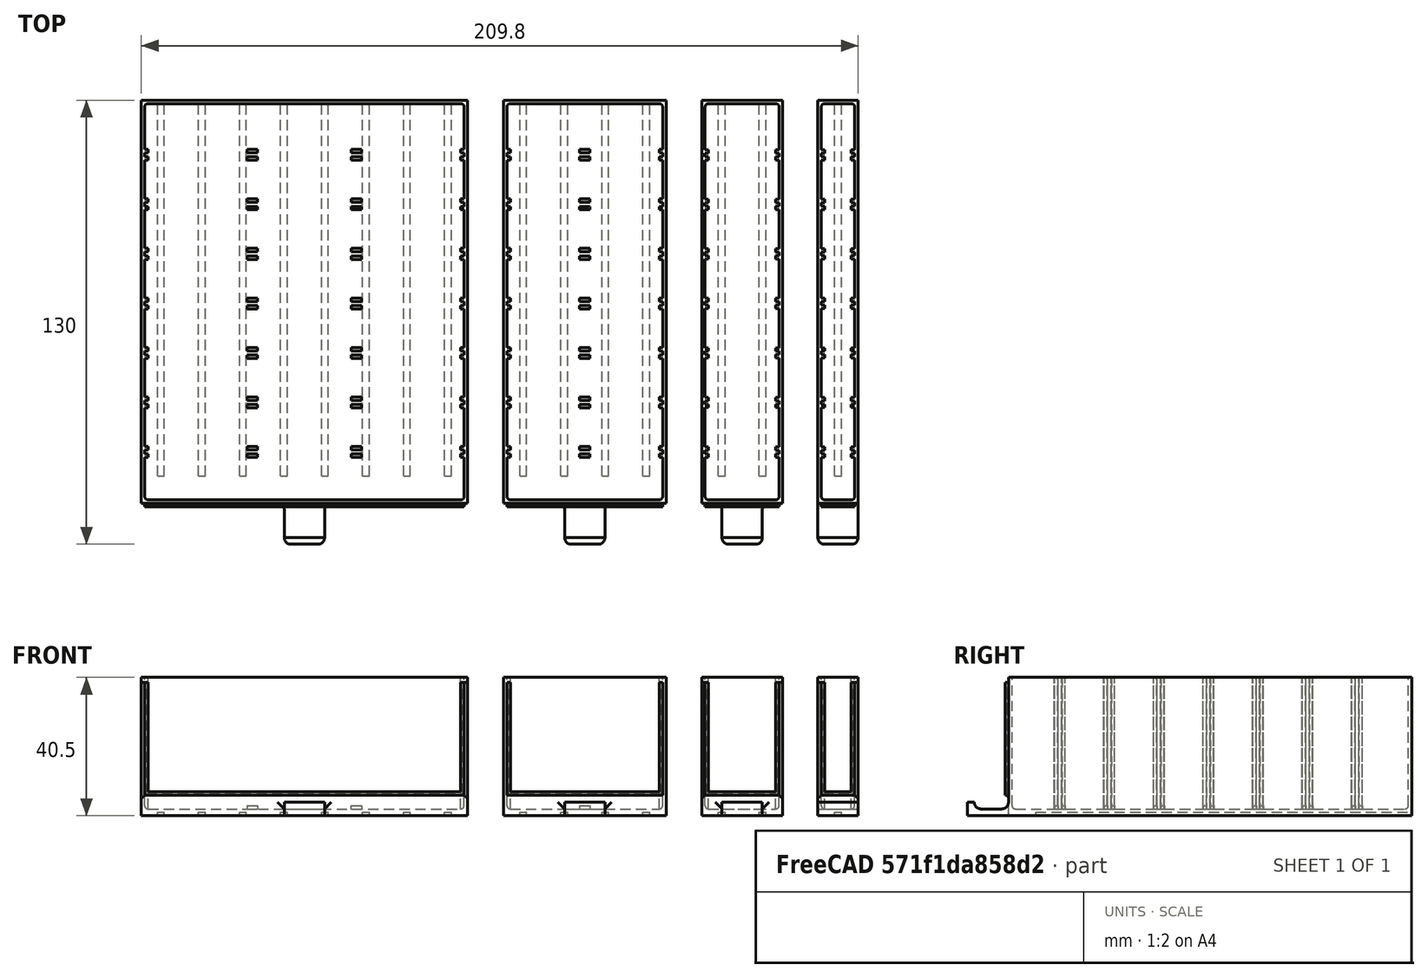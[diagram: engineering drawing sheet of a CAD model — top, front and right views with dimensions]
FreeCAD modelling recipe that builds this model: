
FCSTD DOCUMENT  (FreeCAD 0.16R)
Label: 1story_drawers
License: All rights reserved
LicenseURL: http://en.wikipedia.org/wiki/All_rights_reserved
objects: Part::Box×46, Part::Cut×23, Part::Fillet×19, Part::MultiFuse×19, Part::FeaturePython×8
note: 115 computed .brp shape members not serialized (recipe doc carries the construction recipe); baked Part::Feature solids carry a one-line shape summary decoded from their .brp

FEATURE [Part::Box] Box  label="outer_box"
  Height = 40.5
  Length = 95.5
  Width = 118
FEATURE [Part::Box] Box001  label="inner_box"
  Height = 39.5
  Length = 93.5
  Placement = pos=(1,1,2) rot=(0,0,1;0rad)
  Width = 116
FEATURE [Part::Fillet] Fillet
  Base = -> Box001
  Edges = 8 edges r=1: [Edge1,Edge3,Edge4,Edge5,Edge7,Edge8,Edge9,Edge11]
FEATURE [Part::Cut] Cut  label="Guideless Drawer"
  Base = -> Box
  Tool = -> Fillet
FEATURE [Part::Box] Box004  label="Guide"
  Height = 1
  Length = 2
  Placement = pos=(0,8,0) rot=(0,0,1;0rad)
  Width = 110
FEATURE [Part::FeaturePython] Array  label="Guide array"  # Draft array (typed FeaturePython)
  Angle = 360
  ArrayType = 0
  Axis = (0,0,1)
  Base = -> Box004
  Center = (0,0,0)
  Fuse = false
  IntervalAxis = (0,0,0)
  IntervalX = (12,0,0)
  IntervalY = (0,1,0)
  IntervalZ = (0,0,0)
  NumberPolar = 1
  NumberX = 8
  NumberY = 1
  NumberZ = 1
  Placement = pos=(4.75,0,0) rot=(0,0,1;0rad)
FEATURE [Part::Box] Box006  label="Separator Holder Block"
  Height = 38.5
  Length = 93.5
  Placement = pos=(1,13.4,2) rot=(0,0,1;0rad)
  Width = 3.2
FEATURE [Part::Box] Box007  label="Separator Gap"
  Height = 38.5
  Length = 93.5
  Placement = pos=(1,14.4,2) rot=(0,0,1;0rad)
  Width = 1.2
FEATURE [Part::Box] Box008  label="Separator Holder Gap Block"
  Height = 38.5
  Length = 91.5
  Placement = pos=(2,13.4,2) rot=(0,0,1;0rad)
  Width = 3.2
FEATURE [Part::Fillet] Fillet005
  Base = -> Box006
  Edges = 2 edges r=1: [Edge4,Edge8]
FEATURE [Part::Cut] Cut002  label="Separator Holder Guides"
  Base = -> Fillet005
  Tool = -> Box007
FEATURE [Part::Cut] Cut004  label="Handlerless Guided Drawer"
  Base = -> Cut
  Tool = -> Array
FEATURE [Part::Box] Box009  label="Bottom Separator Holder Gap Block"
  Height = 1
  Length = 3
  Placement = pos=(31,13.4,2) rot=(0,0,1;0rad)
  Width = 3.2
FEATURE [Part::FeaturePython] Array001  label="Bottom Separator Gap Array"  # Draft array (typed FeaturePython)
  Angle = 360
  ArrayType = 0
  Axis = (0,0,1)
  Base = -> Box009
  Center = (0,0,0)
  Fuse = false
  IntervalAxis = (0,0,0)
  IntervalX = (30.5,0,0)
  IntervalY = (0,1,0)
  IntervalZ = (0,0,0)
  NumberPolar = 1
  NumberX = 2
  NumberY = 1
  NumberZ = 1
FEATURE [Part::Cut] Cut005  label="Separator Holder Gap"
  Base = -> Box008
  Tool = -> Array001
FEATURE [Part::Cut] Cut006  label="Separator Holder"
  Base = -> Cut002
  Tool = -> Cut005
FEATURE [Part::FeaturePython] Array002  label="Separator Holder Array"  # Draft array (typed FeaturePython)
  Angle = 360
  ArrayType = 0
  Axis = (0,0,1)
  Base = -> Cut006
  Center = (0,0,0)
  Fuse = false
  IntervalAxis = (0,0,0)
  IntervalX = (1,0,0)
  IntervalY = (0,14.5,0)
  IntervalZ = (0,0,0)
  NumberPolar = 1
  NumberX = 1
  NumberY = 7
  NumberZ = 1
FEATURE [Part::Box] Box010  label="LabelHolder_Main_Block"
  Height = 33
  Length = 93.5
  Placement = pos=(1,-1,6) rot=(0,0,1;0rad)
  Width = 1
  expr: Placement.Base.y = outer_box.Placement.Base.y - LabelHolder_Main_Block.Width
  expr: Placement.Base.x = inner_box.Placement.Base.x
  expr: Length = inner_box.Length
FEATURE [Part::Box] Box011  label="LabelHolder_Inner_Gap"
  Height = 32.5
  Length = 92.5
  Placement = pos=(1.5,-0.5,6.5) rot=(0,0,1;0rad)
  Width = 0.5
  expr: Height = LabelHolder_Main_Block.Height - 0.5mm
  expr: Placement.Base.z = LabelHolder_Main_Block.Placement.Base.z + 0.5mm
  expr: Placement.Base.y = LabelHolder_Main_Block.Placement.Base.y + 0.5mm
  expr: Placement.Base.x = LabelHolder_Main_Block.Placement.Base.x + 0.5mm
  expr: Length = LabelHolder_Main_Block.Length - 1mm
FEATURE [Part::Box] Box012  label="LabelHolder_Outer_Gap"
  Height = 32
  Length = 91.5
  Placement = pos=(2,-1,7) rot=(0,0,1;0rad)
  Width = 0.5
  expr: Height = LabelHolder_Main_Block.Height - 1mm
  expr: Placement.Base.z = LabelHolder_Main_Block.Placement.Base.z + 1mm
  expr: Placement.Base.y = LabelHolder_Main_Block.Placement.Base.y
  expr: Placement.Base.x = LabelHolder_Main_Block.Placement.Base.x + 1mm
  expr: Length = LabelHolder_Main_Block.Length - 2mm
FEATURE [Part::MultiFuse] Fusion003  label="LabelHolder Gap"
  Shapes = -> [Box011,Box012]
FEATURE [Part::Cut] Cut007  label="LabelHolder"
  Base = -> Box010
  Tool = -> Fusion003
FEATURE [Part::MultiFuse] Fusion  label="Handlerless Drawer"
  Shapes = -> [Cut004,Array002]
FEATURE [Part::Box] Box013  label="Handler_block"
  Height = 2
  Length = 11.8
  Placement = pos=(41.85,-12,0) rot=(0,0,1;0rad)
  Width = 12
  expr: Placement.Base.y = outer_box.Placement.Base.y - Handler_block.Width
  expr: Placement.Base.x = outer_box.Placement.Base.x + (outer_box.Length - Handler_block.Length) / 2
FEATURE [Part::Box] Box015  label="Handler_pick"
  Height = 2
  Length = 11.8
  Placement = pos=(41.85,-12,2) rot=(0,0,1;0rad)
  Width = 2
  expr: Placement.Base.z = Handler_block.Placement.Base.z + 2mm
  expr: Placement.Base.y = Handler_block.Placement.Base.y
  expr: Placement.Base.x = Handler_block.Placement.Base.x
FEATURE [Part::MultiFuse] Fusion004
  Shapes = -> [Box015,Box013]
FEATURE [Part::Fillet] Fillet006
  Base = -> Fusion004
  Edges = 5 edges r=1.9: [Edge5,Edge8,Edge10,Edge13,Edge19]
FEATURE [Part::MultiFuse] Fusion005
  Shapes = -> [Fillet006,Fusion]
FEATURE [Part::Fillet] Fillet007  label="LabelHolderlessCabinet"
  Base = -> Fusion005
  Edges = 3 edges r=2: [Edge25,Edge34,Edge39]
FEATURE [Part::MultiFuse] Fusion006
  Shapes = -> [Cut007,Fillet007]
FEATURE [Part::Fillet] Fillet008  label="BigDrawer"
  Base = -> Fusion006
  Edges = 3 edges r=0.9: [Edge11,Edge27,Edge28]
FEATURE [Part::Box] Box016  label="outer_box001"
  Height = 40.5
  Length = 47.6
  Width = 118
FEATURE [Part::Box] Box017  label="inner_box001"
  Height = 39.5
  Length = 45.6
  Placement = pos=(1,1,2) rot=(0,0,1;0rad)
  Width = 116
FEATURE [Part::Fillet] Fillet009
  Base = -> Box017
  Edges = 8 edges r=1: [Edge1,Edge3,Edge4,Edge5,Edge7,Edge8,Edge9,Edge11]
FEATURE [Part::Cut] Cut008  label="Guideless drawer"
  Base = -> Box016
  Tool = -> Fillet009
FEATURE [Part::Box] Box018  label="Guide001"
  Height = 1
  Length = 2
  Placement = pos=(4.8,8,0) rot=(0,0,1;0rad)
  Width = 110
FEATURE [Part::FeaturePython] Array003  label="Guide Array"  # Draft array (typed FeaturePython)
  Angle = 360
  ArrayType = 0
  Axis = (0,0,1)
  Base = -> Box018
  Center = (0,0,0)
  Fuse = false
  IntervalAxis = (0,0,0)
  IntervalX = (12,0,0)
  IntervalY = (0,1,0)
  IntervalZ = (0,0,0)
  NumberPolar = 1
  NumberX = 4
  NumberY = 1
  NumberZ = 1
FEATURE [Part::Box] Box019  label="Separator Block"
  Height = 38.5
  Length = 45.6
  Placement = pos=(1,13.4,2) rot=(0,0,1;0rad)
  Width = 3.2
FEATURE [Part::Box] Box020  label="Separator Gap001"
  Height = 38.5
  Length = 45.6
  Placement = pos=(1,14.4,2) rot=(0,0,1;0rad)
  Width = 1.2
FEATURE [Part::Box] Box021  label="Separator Holder Gap Block001"
  Height = 38.5
  Length = 43.6
  Placement = pos=(2,13.4,2) rot=(0,0,1;0rad)
  Width = 3.2
FEATURE [Part::Fillet] Fillet010
  Base = -> Box019
  Edges = 2 edges r=1: [Edge4,Edge8]
FEATURE [Part::Cut] Cut009  label="Separator Holder Guides001"
  Base = -> Fillet010
  Tool = -> Box020
FEATURE [Part::Cut] Cut010  label="Separatorless Guided Drawer"
  Base = -> Cut008
  Tool = -> Array003
FEATURE [Part::Box] Box022  label="Bottom Separator Holder Gap Block001"
  Height = 1
  Length = 3
  Placement = pos=(22.3,13.4,2) rot=(0,0,1;0rad)
  Width = 3.2
FEATURE [Part::Cut] Cut011  label="Separator Holder Gap001"
  Base = -> Box021
  Tool = -> Box022
FEATURE [Part::Cut] Cut012  label="Separator Holder001"
  Base = -> Cut009
  Tool = -> Cut011
FEATURE [Part::FeaturePython] Array004  label="Separator Holder Array001"  # Draft array (typed FeaturePython)
  Angle = 360
  ArrayType = 0
  Axis = (0,0,1)
  Base = -> Cut012
  Center = (0,0,0)
  Fuse = false
  IntervalAxis = (0,0,0)
  IntervalX = (1,0,0)
  IntervalY = (0,14.5,0)
  IntervalZ = (0,0,0)
  NumberPolar = 1
  NumberX = 1
  NumberY = 7
  NumberZ = 1
FEATURE [Part::Box] Box023  label="LabelHolder_Main_Block001"
  Height = 33
  Length = 45.6
  Placement = pos=(1,-1,6) rot=(0,0,1;0rad)
  Width = 1
  expr: Placement.Base.y = outer_box.Placement.Base.y - LabelHolder_Main_Block.Width
  expr: Placement.Base.x = inner_box.Placement.Base.x
  expr: Length = inner_box.Length
FEATURE [Part::Box] Box024  label="LabelHolder_Inner_Gap001"
  Height = 32.5
  Length = 44.6
  Placement = pos=(1.5,-0.5,6.5) rot=(0,0,1;0rad)
  Width = 0.5
  expr: Placement.Base.y = LabelHolder_Main_Block.Placement.Base.y + 0.5mm
  expr: Height = LabelHolder_Main_Block.Height - 0.5mm
  expr: Placement.Base.z = LabelHolder_Main_Block.Placement.Base.z + 0.5mm
  expr: Length = inner_box.Length - 1mm
FEATURE [Part::Box] Box025  label="LabelHolder_Outer_Gap001"
  Height = 32
  Length = 43.6
  Placement = pos=(2,-1,7) rot=(0,0,1;0rad)
  Width = 0.5
  expr: Placement.Base.y = LabelHolder_Main_Block.Placement.Base.y
  expr: Placement.Base.x = LabelHolder_Main_Block.Placement.Base.x + 1mm
  expr: Length = LabelHolder_Main_Block.Length - 2mm
  expr: Height = LabelHolder_Main_Block.Height - 1mm
  expr: Placement.Base.z = LabelHolder_Main_Block.Placement.Base.z + 1mm
FEATURE [Part::MultiFuse] Fusion007  label="LabelHolder_Gap"
  Shapes = -> [Box024,Box025]
FEATURE [Part::Cut] Cut013  label="LabelHolder001"
  Base = -> Box023
  Tool = -> Fusion007
FEATURE [Part::MultiFuse] Fusion008  label="Handlerless Drawer001"
  Shapes = -> [Array004,Cut010]
FEATURE [Part::Box] Box026  label="Handler_block001"
  Height = 2
  Length = 11.8
  Placement = pos=(17.9,-12,0) rot=(0,0,1;0rad)
  Width = 12
  expr: Placement.Base.y = outer_box.Placement.Base.y - Handler_block.Width
  expr: Placement.Base.x = outer_box.Placement.Base.x + (outer_box.Length - Handler_block.Length) / 2
FEATURE [Part::Box] Box027  label="Handler_pick001"
  Height = 2
  Length = 11.8
  Placement = pos=(17.9,-12,2) rot=(0,0,1;0rad)
  Width = 2
  expr: Placement.Base.z = Handler_block.Placement.Base.z + 2mm
  expr: Placement.Base.y = Handler_block.Placement.Base.y
  expr: Placement.Base.x = Handler_block.Placement.Base.x
FEATURE [Part::MultiFuse] Fusion009
  Shapes = -> [Box026,Box027]
FEATURE [Part::Fillet] Fillet011
  Base = -> Fusion009
  Edges = 5 edges r=1.9: [Edge5,Edge11,Edge15,Edge18,Edge19]
FEATURE [Part::MultiFuse] Fusion010
  Shapes = -> [Fusion008,Fillet011]
FEATURE [Part::Fillet] Fillet012
  Base = -> Fusion010
  Edges = 3 edges r=2: [Edge627,Edge628,Edge629]
FEATURE [Part::MultiFuse] Fusion011  label="StandardDrawer"
  Placement = pos=(106,0,0) rot=(0,0,1;0rad)
  Shapes = -> [Cut013,Fillet012]
FEATURE [Part::Box] Box028  label="outer_box002"
  Height = 40.5
  Length = 23.7
  Width = 118
FEATURE [Part::Box] Box029  label="inner_box002"
  Height = 39.5
  Length = 21.7
  Placement = pos=(1,1,2) rot=(0,0,1;0rad)
  Width = 116
FEATURE [Part::Fillet] Fillet014  label="Filleted Inner Box"
  Base = -> Box029
  Edges = 8 edges r=1: [Edge1,Edge3,Edge4,Edge5,Edge7,Edge8,Edge9,Edge11]
FEATURE [Part::Cut] Cut014  label="Guideless Drawer001"
  Base = -> Box028
  Tool = -> Fillet014
FEATURE [Part::Box] Box030  label="Guide002"
  Height = 1
  Length = 2
  Placement = pos=(0,8,0) rot=(0,0,1;0rad)
  Width = 110
FEATURE [Part::FeaturePython] Array005  label="Guide array001"  # Draft array (typed FeaturePython)
  Angle = 360
  ArrayType = 0
  Axis = (0,0,1)
  Base = -> Box030
  Center = (0,0,0)
  Fuse = false
  IntervalAxis = (0,0,0)
  IntervalX = (12,0,0)
  IntervalY = (0,1,0)
  IntervalZ = (0,0,0)
  NumberPolar = 1
  NumberX = 2
  NumberY = 1
  NumberZ = 1
  Placement = pos=(4.85,0,0) rot=(0,0,1;0rad)
FEATURE [Part::Box] Box031  label="Separator Holder Gap002"
  Height = 38.5
  Length = 21.7
  Placement = pos=(1,14.5,2) rot=(0,0,1;0rad)
  Width = 1
FEATURE [Part::Box] Box032  label="Separator Block001"
  Height = 38.5
  Length = 21.7
  Placement = pos=(1,13.5,2) rot=(0,0,1;0rad)
  Width = 3
FEATURE [Part::Fillet] Fillet015  label="Filletted Separator Block"
  Base = -> Box032
  Edges = 2 edges r=1: [Edge4,Edge8]
FEATURE [Part::Box] Box033  label="Separator Gap002"
  Height = 38.5
  Length = 19.7
  Placement = pos=(2,13.5,2) rot=(0,0,1;0rad)
  Width = 3
FEATURE [Part::Cut] Cut015
  Base = -> Fillet015
  Tool = -> Box033
FEATURE [Part::Cut] Cut003  label="Separator Holder002"
  Base = -> Cut015
  Tool = -> Box031
FEATURE [Part::FeaturePython] Array006  label="Separator Holders Array"  # Draft array (typed FeaturePython)
  Angle = 360
  ArrayType = 0
  Axis = (0,0,1)
  Base = -> Cut003
  Center = (0,0,0)
  Fuse = false
  IntervalAxis = (0,0,0)
  IntervalX = (1,0,0)
  IntervalY = (0,14.5,0)
  IntervalZ = (0,0,0)
  NumberPolar = 1
  NumberX = 1
  NumberY = 7
  NumberZ = 1
FEATURE [Part::Cut] Cut016  label="Guided Drawer"
  Base = -> Cut014
  Tool = -> Array005
FEATURE [Part::Box] Box034  label="LabelHolder_Main_Block002"
  Height = 33
  Length = 21.7
  Placement = pos=(1,-1,6) rot=(0,0,1;0rad)
  Width = 1
  expr: Length = inner_box.Length
  expr: Placement.Base.x = inner_box.Placement.Base.x
  expr: Placement.Base.y = outer_box.Placement.Base.y - LabelHolder_Main_Block.Width
FEATURE [Part::Box] Box035  label="LabelHolder_Inner_Gap002"
  Height = 32.5
  Length = 20.7
  Placement = pos=(1.5,-0.5,6.5) rot=(0,0,1;0rad)
  Width = 0.5
  expr: Length = LabelHolder_Main_Block.Length - 1mm
  expr: Placement.Base.x = LabelHolder_Main_Block.Placement.Base.x + (LabelHolder_Main_Block.Length - LabelHolder_Inner_Gap.Length) / 2
  expr: Placement.Base.y = LabelHolder_Main_Block.Placement.Base.y + LabelHolder_Inner_Gap.Width
  expr: Width = LabelHolder_Main_Block.Width / 2
  expr: Height = LabelHolder_Main_Block.Height - 0.5mm
  expr: Placement.Base.z = LabelHolder_Main_Block.Placement.Base.z + 0.5mm
FEATURE [Part::Box] Box036  label="LabelHolder_Outer_Gap002"
  Height = 32
  Length = 19.7
  Placement = pos=(2,-1,7) rot=(0,0,1;0rad)
  Width = 0.5
  expr: Placement.Base.y = LabelHolder_Inner_Gap.Placement.Base.y - LabelHolder_Outer_Gap.Width
  expr: Placement.Base.x = LabelHolder_Main_Block.Placement.Base.x + (LabelHolder_Main_Block.Length - LabelHolder_Outer_Gap.Length) / 2
  expr: Placement.Base.z = LabelHolder_Main_Block.Placement.Base.z + 1mm
  expr: Height = LabelHolder_Main_Block.Height - 1mm
  expr: Width = LabelHolder_Main_Block.Width / 2
  expr: Length = LabelHolder_Main_Block.Length - 2mm
FEATURE [Part::MultiFuse] Fusion012  label="LabelHolder_Gap001"
  Shapes = -> [Box035,Box036]
FEATURE [Part::Cut] Cut017  label="LabelHolder002"
  Base = -> Box034
  Tool = -> Fusion012
FEATURE [Part::MultiFuse] Fusion013  label="Handlerless Drawer002"
  Shapes = -> [Cut016,Array006]
FEATURE [Part::Box] Box037  label="Handler_block002"
  Height = 2
  Length = 11.8
  Placement = pos=(5.95,-12,0) rot=(0,0,1;0rad)
  Width = 12
  expr: Placement.Base.x = (outer_box.Length - Handler_block.Length) / 2
FEATURE [Part::Box] Box014  label="Handler_pick002"
  Height = 2
  Length = 11.8
  Placement = pos=(5.95,-12,2) rot=(0,0,1;0rad)
  Width = 2
  expr: Placement.Base.z = Handler_block.Placement.Base.z + 2mm
  expr: Placement.Base.y = Handler_block.Placement.Base.y
  expr: Placement.Base.x = Handler_block.Placement.Base.x
FEATURE [Part::MultiFuse] Fusion014
  Shapes = -> [Box014,Box037]
FEATURE [Part::Fillet] Fillet016  label="Handler"
  Base = -> Fusion014
  Edges = 5 edges r=1.9: [Edge5,Edge8,Edge10,Edge13,Edge19]
FEATURE [Part::MultiFuse] Fusion015
  Shapes = -> [Fusion013,Fillet016]
FEATURE [Part::Fillet] Fillet017  label="LabelHolderlessDrawer"
  Base = -> Fusion015
  Edges = 3 edges r=2: [Edge6,Edge7,Edge8]
FEATURE [Part::MultiFuse] Fusion016
  Shapes = -> [Cut017,Fillet017]
FEATURE [Part::Fillet] Fillet018  label="SmallDrawer"
  Base = -> Fusion016
  Edges = 3 edges r=0.9: [Edge11,Edge27,Edge28]
  Placement = pos=(164,0,0) rot=(0,0,1;0rad)
FEATURE [Part::Box] Box038  label="outer_box003"
  Height = 40.5
  Length = 11.8
  Width = 118
FEATURE [Part::Box] Box039  label="inner_box003"
  Height = 38.5
  Length = 9.8
  Placement = pos=(1,1,2) rot=(0,0,1;0rad)
  Width = 116
FEATURE [Part::Fillet] Fillet019
  Base = -> Box039
  Edges = 8 edges r=1: [Edge1,Edge3,Edge4,Edge5,Edge7,Edge8,Edge9,Edge11]
FEATURE [Part::Cut] Cut018  label="Guideless Drawer002"
  Base = -> Box038
  Tool = -> Fillet019
FEATURE [Part::Box] Box040  label="Guide003"
  Height = 1
  Length = 2
  Placement = pos=(4.9,8,0) rot=(0,0,1;0rad)
  Width = 110
FEATURE [Part::Box] Box041  label="Separator Holder Block Draft"
  Height = 38.5
  Length = 9.8
  Width = 3
FEATURE [Part::Box] Box042  label="Separator Gap003"
  Height = 38.5
  Length = 9.8
  Placement = pos=(0,1,0) rot=(0,0,1;0rad)
  Width = 1
FEATURE [Part::Box] Box043  label="Separator Holder Gap003"
  Height = 38.5
  Length = 7.8
  Placement = pos=(1,0,0) rot=(0,0,1;0rad)
  Width = 3
FEATURE [Part::Fillet] Fillet020
  Base = -> Box041
  Edges = 2 edges r=1: [Edge4,Edge8]
FEATURE [Part::Cut] Cut019
  Base = -> Fillet020
  Tool = -> Box042
FEATURE [Part::Cut] Cut020  label="Separator Holder Draft"
  Base = -> Cut019
  Tool = -> Box043
FEATURE [Part::FeaturePython] Array007  label="Separator Holder Array002"  # Draft array (typed FeaturePython)
  Angle = 360
  ArrayType = 0
  Axis = (0,0,1)
  Base = -> Cut020
  Center = (0,0,0)
  Fuse = false
  IntervalAxis = (0,0,0)
  IntervalX = (1,0,0)
  IntervalY = (0,14.5,0)
  IntervalZ = (0,0,0)
  NumberPolar = 1
  NumberX = 1
  NumberY = 7
  NumberZ = 1
  Placement = pos=(1,13.5,2) rot=(0,0,1;0rad)
FEATURE [Part::Cut] Cut021  label="Guided Separatorless Drawer"
  Base = -> Cut018
  Tool = -> Box040
FEATURE [Part::Box] Box044  label="labelholder_main_block"
  Height = 33
  Length = 9.8
  Placement = pos=(1,-1,6) rot=(0,0,1;0rad)
  Width = 1
FEATURE [Part::Box] Box045  label="labelholder_inner_gap"
  Height = 32.5
  Length = 8.8
  Placement = pos=(1.5,-0.5,6.5) rot=(0,0,1;0rad)
  Width = 0.5
  expr: Height = labelholder_main_block.Height - 0.5mm
  expr: Placement.Base.z = labelholder_main_block.Placement.Base.z + 0.5mm
FEATURE [Part::Box] Box046  label="LabelHolder Outer Gap"
  Height = 32
  Length = 7.8
  Placement = pos=(2,-1,7) rot=(0,0,1;0rad)
  Width = 0.5
  expr: Height = labelholder_main_block.Height - 1mm
  expr: Placement.Base.z = labelholder_main_block.Placement.Base.z + 1mm
FEATURE [Part::Cut] Cut022
  Base = -> Box044
  Tool = -> Box045
FEATURE [Part::Cut] Cut023  label="Label Holder"
  Base = -> Cut022
  Tool = -> Box046
FEATURE [Part::MultiFuse] Fusion017  label="Separator Holdered Drawer"
  Shapes = -> [Cut021,Array007]
FEATURE [Part::Box] Box047  label="HandlerBlock"
  Height = 2
  Length = 11.8
  Placement = pos=(0,-12,0) rot=(0,0,1;0rad)
  Width = 12
FEATURE [Part::Box] Box048  label="Cube"
  Height = 2
  Length = 11.8
  Placement = pos=(0,-12,2) rot=(0,0,1;0rad)
  Width = 2
FEATURE [Part::MultiFuse] Fusion001
  Shapes = -> [Box048,Box047]
FEATURE [Part::Fillet] Fillet021
  Base = -> Fusion001
  Edges = 5 edges r=1.9: [Edge5,Edge8,Edge10,Edge13,Edge19]
FEATURE [Part::MultiFuse] Fusion002
  Shapes = -> [Fillet021,Fusion017]
FEATURE [Part::Fillet] Fillet022
  Base = -> Fusion002
  Edges = 1 edges r=2: [Edge42]
FEATURE [Part::MultiFuse] Fusion018
  Shapes = -> [Cut023,Fillet022]
FEATURE [Part::Fillet] Fillet023  label="TinyDrawer"
  Base = -> Fusion018
  Edges = 3 edges r=0.9: [Edge11,Edge27,Edge28]
  Placement = pos=(198,0,0) rot=(0,0,1;0rad)
